# Revit family: Fireplace_Wood_Majestic_Ashland
name_source: partatom
category: Mechanical Equipment
revit_build: Autodesk Revit 2018 (Build: 20170223_1515(x64)
units: mm (PartAtom-declared; Revit-internal decimal feet)

## family parameters
Cut with Voids When Loaded = No
Host = Face
OmniClass Number = 23.40.20.34.14.11
OmniClass Title = Fireplace Inserts
Part Type = Normal
Room Calculation Point = No
Round Connector Dimension = Use Radius
Shared = No

## types (2) — shared parameters
Assembly Code = D3020
Default Elevation = 0' - 0"
Efficiency Ratings = Determined by Wood Used
Fixture Finish = Metal - Hearth n Home - Metallic Black
Fuel Consumption = as Specified
Green Building-LEED = http://www.arcat.com
HVAC_BTU Input = 0.0 Btu/h
HVAC_BTU Output = 0.0 Btu/h
Heating Capacity = as Specified
Keynote = 10305
Manufacturer = Majestic
Manufacturer Website = http://www.majesticproducts.com
Model = ASH42
Opening Height = 3' - 2"
Opening Width = 3' - 6"
Product Data = http://www.arcat.com
Product Properties = http://www.majesticproducts.com
Rear Width = 3' - 1 1/8"
Revision = R1_2017-04
Sales Information = http://www.majesticproducts.com
Standards Conformance = UL 127  ;  ULC-S610
URL = http://www.majesticproducts.com
Unit Depth = 2' - 3 1/2"
Unit Height = 6' - 2 1/8"
Unit Width = 4' - 4 7/8"
zero-valued in all types: Expected Lifespan (Years), Maintenance Schedule (Months), Unit Weight, Warranty Duration (Years)

## per-type parameters (varying)
| type | Description | Fuel Type |
| 42 x 38 Viewing Area Gas Burning | Majestic Gas Burning Fireplace - Ashland ASH42 as Specified | NG or LP |
| 42 x 38 Viewing Area Wood Burning | Majestic Wood Burning Fireplace - Ashland ASH42 as Specified | Wood |

## geometry (parser evidence)
native form markers: Sweep x5
no freeform markers — native parametric forms only
